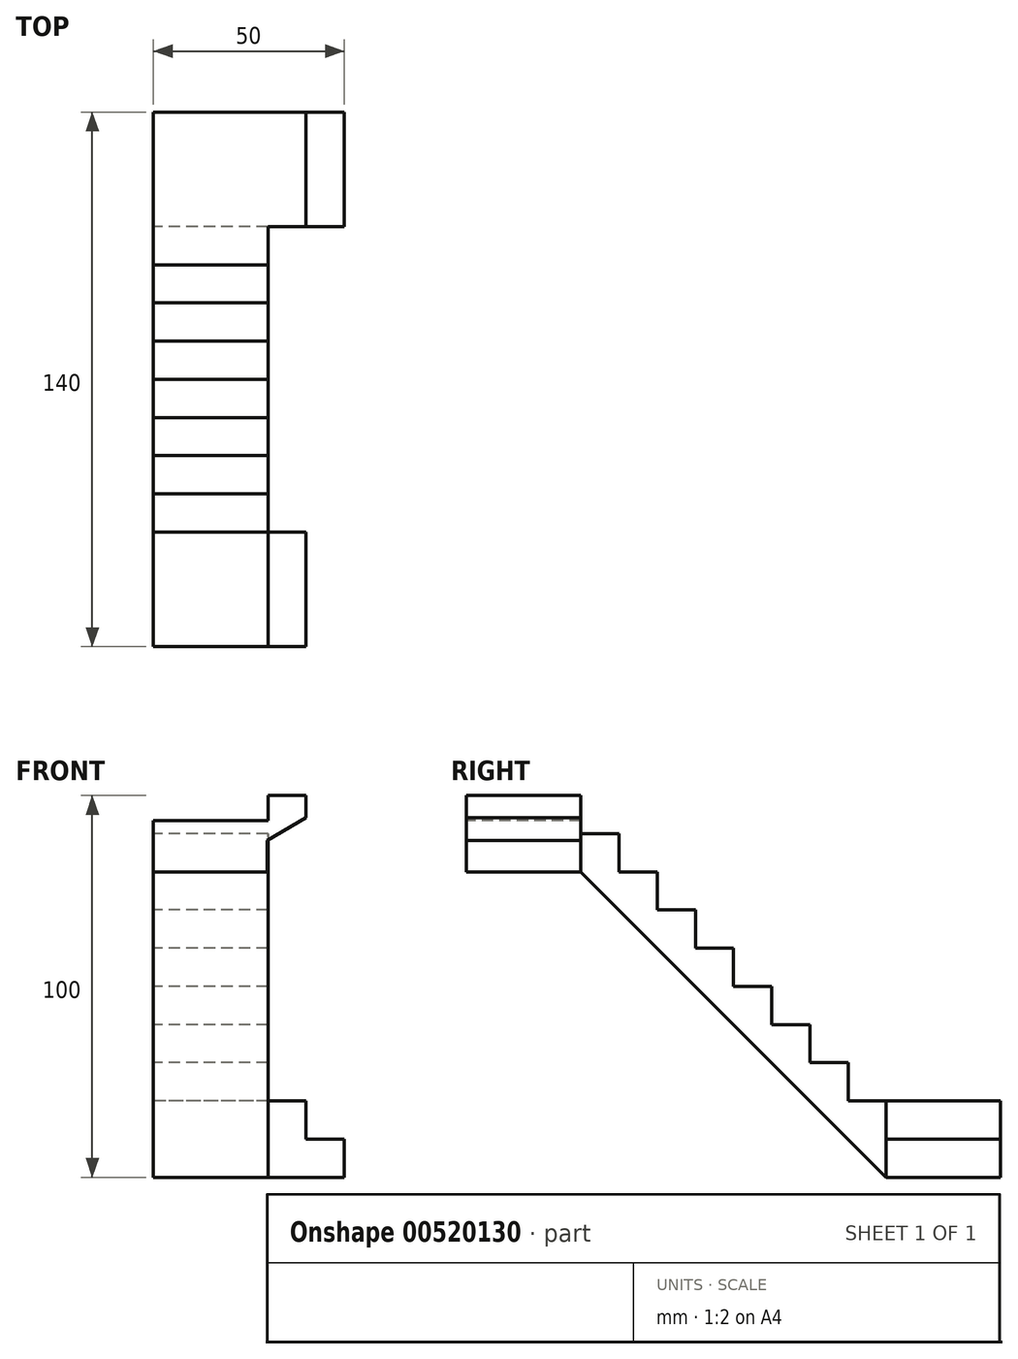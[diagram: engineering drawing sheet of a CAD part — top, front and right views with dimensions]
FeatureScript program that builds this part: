
annotation { "Feature Type Name" : "Feature", "Feature Type Description" : "" }
export const myFeature = defineFeature(function(context is Context, id is Id, definition is map)
    precondition{}
    {
        {
            var Q0;
            Q0=qCreatedBy(makeId("Top.planeOp"),FACE);
            var sketch = newSketch(context, id + "F0", { "sketchPlane" : qUnion([Q0])});
            skLineSegment(sketch, "E0.bottom", {"start": v(-33.35, 59.94) * mm, "end": v(16.65, 59.94) * mm});
            skLineSegment(sketch, "E0.top", {"start": v(-3.35, 29.94) * mm, "end": v(16.65, 29.94) * mm});
            skLineSegment(sketch, "E0.left", {"start": v(-33.35, 59.94) * mm, "end": v(-33.35, 29.94) * mm});
            skLineSegment(sketch, "E0.right", {"start": v(16.65, 59.94) * mm, "end": v(16.65, 29.94) * mm});
            skLineSegment(sketch, "E1.left", {"start": v(-33.35, 29.94) * mm, "end": v(-33.35, -50.06) * mm});
            skLineSegment(sketch, "E1.right", {"start": v(-3.35, 29.94) * mm, "end": v(-3.35, -50.06) * mm});
            skLineSegment(sketch, "E2.bottom", {"start": v(-3.35, -50.06) * mm, "end": v(16.65, -50.06) * mm});
            skLineSegment(sketch, "E2.top", {"start": v(-33.35, -80.06) * mm, "end": v(16.65, -80.06) * mm});
            skLineSegment(sketch, "E2.left", {"start": v(-33.35, -50.06) * mm, "end": v(-33.35, -80.06) * mm});
            skLineSegment(sketch, "E2.right", {"start": v(16.65, -50.06) * mm, "end": v(16.65, -80.06) * mm});
            skSolve(sketch);
        }
        {
            var Q0;
            Q0=makeQuery(id+"F0.imprint","IMPRINT",FACE,{"disambiguationData":[TD([[makeQuery(id+"F0.imprint","IMPRINT",EDGE,{"derivedFrom":sQuery(id+"F0.wireOp",EDGE,"E0.bottom")}),-1.0]])]});
            extrude(context, id + "F1", {"entities" : qUnion([Q0]), "depth" : 120 * mm, "offsetDistance" : 25 * mm});
        }
        {
            var Q0;
            Q0=makeQuery(id+"F1.opExtrude","SWEPT_FACE",FACE,{"disambiguationData":[OSD([sQuery(id+"F0.wireOp",EDGE,"E0.bottom")])]});
            var sketch = newSketch(context, id + "F2", { "sketchPlane" : qUnion([Q0])});
            skLineSegment(sketch, "E3.bottom", {"start": v(-16.65, 10) * mm, "end": v(-6.65, 10) * mm});
            skLineSegment(sketch, "E3.top", {"start": v(-16.65, 20) * mm, "end": v(-6.65, 20) * mm});
            skLineSegment(sketch, "E3.left", {"start": v(-16.65, 10) * mm, "end": v(-16.65, 20) * mm});
            skLineSegment(sketch, "E3.right", {"start": v(-6.65, 10) * mm, "end": v(-6.65, 20) * mm});
            skLineSegment(sketch, "E4.bottom", {"start": v(-6.65, 20) * mm, "end": v(3.35, 20) * mm});
            skLineSegment(sketch, "E4.top", {"start": v(-6.65, 30) * mm, "end": v(3.35, 30) * mm});
            skLineSegment(sketch, "E4.left", {"start": v(-6.65, 20) * mm, "end": v(-6.65, 30) * mm});
            skLineSegment(sketch, "E4.right", {"start": v(3.35, 20) * mm, "end": v(3.35, 30) * mm});
            skLineSegment(sketch, "E5", {"start": v(3.35, 30) * mm, "end": v(3.35, 120) * mm});
            skSolve(sketch);
        }
        {
            var Q0;
            Q0 = qSketchRegion(id + "F2", true);
            var Q1;
            {var subQ1=sQuery(id+"F2.wireOp",EDGE,"E3.top");Q1=makeQuery(id+"F2.imprint","IMPRINT",FACE,{"disambiguationData":[TD([[makeQuery(id+"F2.imprint","IMPRINT",EDGE,{"derivedFrom":subQ1}),1.0]])]});}
            extrude(context, id + "F3", {"entities" : qUnion([Q0, Q1]), "operationType" : NewBodyOperationType.REMOVE, "oppositeDirection" : true, "depth" : 30 * mm, "offsetDistance" : 25 * mm});
        }
        {
            var Q0;
            Q0=makeQuery(id+"F3.boolean.opBoolean","MERGE",FACE,{"derivedFrom":[makeQuery(id+"F1.opExtrude","SWEPT_FACE",FACE,{"disambiguationData":[OSD([sQuery(id+"F0.wireOp",EDGE,"E1.right")])]}),makeQuery(id+"F3.opExtrude","SWEPT_FACE",FACE,{"disambiguationData":[OSD([sQuery(id+"F2.wireOp",EDGE,"E4.right"),sQuery(id+"F2.wireOp",EDGE,"E5")])]})]});
            var sketch = newSketch(context, id + "F4", { "sketchPlane" : qUnion([Q0])});
            skLineSegment(sketch, "E6", {"start": v(29.94, 20) * mm, "end": v(-50.06, 100) * mm});
            skLineSegment(sketch, "E7", {"start": v(-50.06, 100) * mm, "end": v(-50.06, 120) * mm});
            skLineSegment(sketch, "E8", {"start": v(-50.06, 120) * mm, "end": v(29.94, 120) * mm});
            skLineSegment(sketch, "E9", {"start": v(29.94, 120) * mm, "end": v(29.94, 20) * mm});
            skSolve(sketch);
        }
        {
            var Q0;
            Q0=makeQuery(id+"F4.imprint","IMPRINT",FACE,{"disambiguationData":[TD([[makeQuery(id+"F4.imprint","IMPRINT",EDGE,{"derivedFrom":sQuery(id+"F4.wireOp",EDGE,"E6")}),-1.0]])]});
            extrude(context, id + "F5", {"entities" : qUnion([Q0]), "operationType" : NewBodyOperationType.REMOVE, "oppositeDirection" : true, "depth" : 30 * mm, "offsetDistance" : 25 * mm});
        }
        {
            var Q0;
            {var subQ0=sQuery(id+"F0.wireOp",EDGE,"E1.right");var subQ1=makeQuery(id+"F1.opExtrude","SWEPT_FACE",FACE,{"disambiguationData":[OSD([subQ0])]});var subQ3=sQuery(id+"F0.wireOp",EDGE,"E0.bottom");var subQ4=makeQuery(id+"F3.opExtrude","SWEPT_FACE",FACE,{"disambiguationData":[OSD([sQuery(id+"F2.wireOp",EDGE,"E4.right"),sQuery(id+"F2.wireOp",EDGE,"E5")])]});Q0=makeQuery(id+"F5.boolean.opBoolean","SPLIT",FACE,{"disambiguationData":[TD([makeQuery(id+"F1.opExtrude","SWEPT_FACE",FACE,{"disambiguationData":[OSD([subQ3])]})])],"derivedFrom":makeQuery(id+"F3.boolean.opBoolean","MERGE",FACE,{"derivedFrom":[subQ1,subQ4]})});}
            var sketch = newSketch(context, id + "F6", { "sketchPlane" : qUnion([Q0])});
            skLineSegment(sketch, "E10", {"start": v(29.94, 20) * mm, "end": v(59.94, 20) * mm});
            skLineSegment(sketch, "E11", {"start": v(59.94, 20) * mm, "end": v(59.94, 120) * mm});
            skLineSegment(sketch, "E12", {"start": v(59.94, 120) * mm, "end": v(29.94, 120) * mm});
            skLineSegment(sketch, "E13", {"start": v(29.94, 120) * mm, "end": v(29.94, 20) * mm});
            skSolve(sketch);
        }
        {
            var Q0;
            Q0 = qSketchRegion(id + "F6", true);
            extrude(context, id + "F7", {"entities" : qUnion([Q0]), "operationType" : NewBodyOperationType.REMOVE, "oppositeDirection" : true, "depth" : 30 * mm, "offsetDistance" : 25 * mm});
        }
        {
            var Q0;
            Q0=makeQuery(id+"F1.opExtrude","SWEPT_FACE",FACE,{"disambiguationData":[OSD([sQuery(id+"F0.wireOp",EDGE,"E0.left"),sQuery(id+"F0.wireOp",EDGE,"E1.left"),sQuery(id+"F0.wireOp",EDGE,"E2.left")])]});
            var sketch = newSketch(context, id + "F8", { "sketchPlane" : qUnion([Q0])});
            skLineSegment(sketch, "E14", {"start": v(-29.94, 20) * mm, "end": v(-29.94, 0) * mm});
            skLineSegment(sketch, "E15", {"start": v(-29.94, 0) * mm, "end": v(50.06, 80) * mm});
            skLineSegment(sketch, "E16", {"start": v(50.06, 80) * mm, "end": v(50.06, 100) * mm});
            skLineSegment(sketch, "E17", {"start": v(50.06, 80) * mm, "end": v(80.06, 80) * mm});
            skSolve(sketch);
        }
        {
            var Q0;
            Q0 = qSketchRegion(id + "F8", true);
            var Q1;
            {var subQ0=sQuery(id+"F8.wireOp",EDGE,"E15");Q1=makeQuery(id+"F8.imprint","IMPRINT",FACE,{"disambiguationData":[TD([[makeQuery(id+"F8.imprint","IMPRINT",EDGE,{"derivedFrom":subQ0}),-1.0]])]});}
            extrude(context, id + "F9", {"entities" : qUnion([Q0, Q1]), "operationType" : NewBodyOperationType.REMOVE, "oppositeDirection" : true, "depth" : 60 * mm, "offsetDistance" : 25 * mm});
        }
        {
            var Q0;
            Q0=makeQuery(id+"F1.opExtrude","SWEPT_FACE",FACE,{"disambiguationData":[OSD([sQuery(id+"F0.wireOp",EDGE,"E0.left"),sQuery(id+"F0.wireOp",EDGE,"E1.left"),sQuery(id+"F0.wireOp",EDGE,"E2.left")])]});
            var sketch = newSketch(context, id + "F10", { "sketchPlane" : qUnion([Q0])});
            skLineSegment(sketch, "E18.bottom", {"start": v(-29.94, 20) * mm, "end": v(-19.94, 20) * mm});
            skLineSegment(sketch, "E18.top", {"start": v(-29.94, 30) * mm, "end": v(-19.94, 30) * mm});
            skLineSegment(sketch, "E18.left", {"start": v(-29.94, 20) * mm, "end": v(-29.94, 30) * mm});
            skLineSegment(sketch, "E18.right", {"start": v(-19.94, 20) * mm, "end": v(-19.94, 30) * mm});
            skLineSegment(sketch, "E19.bottom", {"start": v(-19.94, 30) * mm, "end": v(-9.94, 30) * mm});
            skLineSegment(sketch, "E19.top", {"start": v(-19.94, 40) * mm, "end": v(-9.94, 40) * mm});
            skLineSegment(sketch, "E19.left", {"start": v(-19.94, 30) * mm, "end": v(-19.94, 40) * mm});
            skLineSegment(sketch, "E19.right", {"start": v(-9.94, 30) * mm, "end": v(-9.94, 40) * mm});
            skLineSegment(sketch, "E20.bottom", {"start": v(-9.94, 40) * mm, "end": v(0.06, 40) * mm});
            skLineSegment(sketch, "E20.top", {"start": v(-9.94, 50) * mm, "end": v(0.06, 50) * mm});
            skLineSegment(sketch, "E20.left", {"start": v(-9.94, 40) * mm, "end": v(-9.94, 50) * mm});
            skLineSegment(sketch, "E20.right", {"start": v(0.06, 40) * mm, "end": v(0.06, 50) * mm});
            skLineSegment(sketch, "E21.bottom", {"start": v(0.06, 50) * mm, "end": v(10.06, 50) * mm});
            skLineSegment(sketch, "E21.top", {"start": v(0.06, 60) * mm, "end": v(10.06, 60) * mm});
            skLineSegment(sketch, "E21.left", {"start": v(0.06, 50) * mm, "end": v(0.06, 60) * mm});
            skLineSegment(sketch, "E21.right", {"start": v(10.06, 50) * mm, "end": v(10.06, 60) * mm});
            skLineSegment(sketch, "E22.bottom", {"start": v(10.06, 60) * mm, "end": v(20.06, 60) * mm});
            skLineSegment(sketch, "E22.top", {"start": v(10.06, 70) * mm, "end": v(20.06, 70) * mm});
            skLineSegment(sketch, "E22.left", {"start": v(10.06, 60) * mm, "end": v(10.06, 70) * mm});
            skLineSegment(sketch, "E22.right", {"start": v(20.06, 60) * mm, "end": v(20.06, 70) * mm});
            skLineSegment(sketch, "E23.top", {"start": v(40.06, 100) * mm, "end": v(50.06, 100) * mm});
            skLineSegment(sketch, "E23.left", {"start": v(40.06, 90) * mm, "end": v(40.06, 100) * mm});
            skLineSegment(sketch, "E23.right", {"start": v(50.06, 90) * mm, "end": v(50.06, 100) * mm});
            skLineSegment(sketch, "E24", {"start": v(40.06, 90) * mm, "end": v(50.06, 90) * mm});
            skLineSegment(sketch, "E25.bottom", {"start": v(20.06, 70) * mm, "end": v(30.06, 70) * mm});
            skLineSegment(sketch, "E25.top", {"start": v(20.06, 80) * mm, "end": v(30.06, 80) * mm});
            skLineSegment(sketch, "E25.left", {"start": v(20.06, 70) * mm, "end": v(20.06, 80) * mm});
            skLineSegment(sketch, "E25.right", {"start": v(30.06, 70) * mm, "end": v(30.06, 80) * mm});
            skLineSegment(sketch, "E26.bottom", {"start": v(30.06, 80) * mm, "end": v(40.06, 80) * mm});
            skLineSegment(sketch, "E26.top", {"start": v(30.06, 90) * mm, "end": v(40.06, 90) * mm});
            skLineSegment(sketch, "E26.left", {"start": v(30.06, 80) * mm, "end": v(30.06, 90) * mm});
            skLineSegment(sketch, "E26.right", {"start": v(40.06, 80) * mm, "end": v(40.06, 90) * mm});
            skSolve(sketch);
        }
        {
            var Q0;
            Q0 = qSketchRegion(id + "F10", true);
            extrude(context, id + "F11", {"entities" : qUnion([Q0]), "operationType" : NewBodyOperationType.REMOVE, "oppositeDirection" : true, "depth" : 30 * mm, "offsetDistance" : 25 * mm});
        }
        {
            var Q0;
            Q0=makeQuery(id+"F1.opExtrude","SWEPT_FACE",FACE,{"disambiguationData":[OSD([sQuery(id+"F0.wireOp",EDGE,"E2.top")])]});
            var sketch = newSketch(context, id + "F12", { "sketchPlane" : qUnion([Q0])});
            skLineSegment(sketch, "E27.bottom", {"start": v(16.65, 120) * mm, "end": v(6.65, 120) * mm});
            skLineSegment(sketch, "E27.top", {"start": v(16.65, 110) * mm, "end": v(6.65, 110) * mm});
            skLineSegment(sketch, "E27.left", {"start": v(16.65, 120) * mm, "end": v(16.65, 110) * mm});
            skLineSegment(sketch, "E27.right", {"start": v(6.65, 120) * mm, "end": v(6.65, 110) * mm});
            skLineSegment(sketch, "E28.bottom", {"start": v(6.65, 110) * mm, "end": v(-3.35, 110) * mm});
            skLineSegment(sketch, "E28.top", {"start": v(6.65, 100) * mm, "end": v(-3.35, 100) * mm});
            skLineSegment(sketch, "E28.left", {"start": v(6.65, 110) * mm, "end": v(6.65, 100) * mm});
            skLineSegment(sketch, "E28.right", {"start": v(-3.35, 110) * mm, "end": v(-3.35, 100) * mm});
            skLineSegment(sketch, "E29", {"start": v(-3.5, 80) * mm, "end": v(-3.5, 88.2) * mm});
            skLineSegment(sketch, "E30", {"start": v(-3.5, 88.2) * mm, "end": v(16.65, 100) * mm});
            skLineSegment(sketch, "E31", {"start": v(-3.35, 110) * mm, "end": v(-3.35, 120) * mm});
            skSolve(sketch);
        }
        {
            var Q0;
            Q0 = qSketchRegion(id + "F12", true);
            var Q1;
            {var subQ0=sQuery(id+"F12.wireOp",EDGE,"E29");Q1=makeQuery(id+"F12.imprint","IMPRINT",FACE,{"disambiguationData":[TD([[makeQuery(id+"F12.imprint","IMPRINT",EDGE,{"derivedFrom":subQ0}),-1.0]])]});}
            var Q2;
            {var subQ0=sQuery(id+"F12.wireOp",EDGE,"E27.right");Q2=makeQuery(id+"F12.imprint","IMPRINT",FACE,{"disambiguationData":[TD([[makeQuery(id+"F12.imprint","IMPRINT",EDGE,{"derivedFrom":subQ0}),-1.0]])]});}
            extrude(context, id + "F13", {"entities" : qUnion([Q0, Q1, Q2]), "operationType" : NewBodyOperationType.REMOVE, "oppositeDirection" : true, "depth" : 30 * mm, "offsetDistance" : 25 * mm});
        }
        {
            var Q0;
            Q0=makeQuery(id+"F1.opExtrude","SWEPT_FACE",FACE,{"disambiguationData":[OSD([sQuery(id+"F0.wireOp",EDGE,"E2.top")])]});
            var sketch = newSketch(context, id + "F14", { "sketchPlane" : qUnion([Q0])});
            skLineSegment(sketch, "E32.top", {"start": v(-3.5, 120) * mm, "end": v(-33.35, 120) * mm});
            skLineSegment(sketch, "E32.right", {"start": v(-33.35, 93.37) * mm, "end": v(-33.35, 120) * mm});
            skLineSegment(sketch, "E33", {"start": v(-33.35, 93.37) * mm, "end": v(-3.35, 93.37) * mm});
            skLineSegment(sketch, "E34", {"start": v(-3.35, 93.37) * mm, "end": v(-3.35, 120) * mm});
            skSolve(sketch);
        }
        {
            var Q0;
            Q0 = qSketchRegion(id + "F14", true);
            var Q1;
            {var subQ3=sQuery(id+"F14.wireOp",EDGE,"E32.top");Q1=makeQuery(id+"F14.imprint","IMPRINT",FACE,{"disambiguationData":[TD([[makeQuery(id+"F14.imprint","IMPRINT",EDGE,{"derivedFrom":subQ3}),-1.0]])]});}
            extrude(context, id + "F15", {"entities" : qUnion([Q0, Q1]), "operationType" : NewBodyOperationType.REMOVE, "oppositeDirection" : true, "depth" : 30 * mm, "offsetDistance" : 25 * mm});
        }
        {
            var Q0;
            Q0=makeQuery(id+"F1.opExtrude","SWEPT_FACE",FACE,{"disambiguationData":[OSD([sQuery(id+"F0.wireOp",EDGE,"E2.top")])]});
            var sketch = newSketch(context, id + "F16", { "sketchPlane" : qUnion([Q0])});
            skLineSegment(sketch, "E35.bottom", {"start": v(6.65, 110) * mm, "end": v(16.65, 110) * mm});
            skLineSegment(sketch, "E35.top", {"start": v(6.65, 86.42) * mm, "end": v(16.65, 86.42) * mm});
            skLineSegment(sketch, "E35.left", {"start": v(6.65, 110) * mm, "end": v(6.65, 86.42) * mm});
            skLineSegment(sketch, "E35.right", {"start": v(16.65, 110) * mm, "end": v(16.65, 86.42) * mm});
            skSolve(sketch);
        }
        {
            var Q0;
            Q0 = qSketchRegion(id + "F16", true);
            extrude(context, id + "F17", {"entities" : qUnion([Q0]), "operationType" : NewBodyOperationType.REMOVE, "oppositeDirection" : true, "depth" : 30 * mm, "offsetDistance" : 25 * mm});
        }
    });
